# Revit family: Дверь RW 64 двустворчатая. Окрывание наружу
name_source: partatom
category: Окна
revit_build: Autodesk Revit 2016 (Build: 20160314_0715(x64)
units: mm (PartAtom-declared; Revit-internal decimal feet)

## family parameters
Всегда вертикально = Да
Заголовок OmniClass = Windows
Номер OmniClass = 23.30.20.00
Общий = Нет
Основа = Стена
При загрузке вырезать с полостями = Нет
Точка расчета площади = Нет

## types (2) — shared parameters
ADSK_Версия Revit = Revit 2016
ADSK_Единица измерения = шт.
ADSK_Наименование краткое = Дверь RW 64 двустворчатая
Rед = 1.0000 (м²·K)/Вт
Rпрофиля = 1.0000 (м²·K)/Вт
Rстеклопакета = 1.0000 (м²·K)/Вт
URL = http://www.realit.ru
λ краевой зоны стеклопакета = 0.0000 (м²·K)/Вт
Аналитическая конструкция = <Нет>
Высота подоконника по умолчанию = 50 мм
Зазор между створок = 9 мм
Замыкание стены = По основе
Изготовитель = REALIT
Материал-Отлив = REALIT_Отлив_Белый
Материал-Подоконник = REALIT_ПВХ_Белый
Материал-Рама = REALIT_Профиль_RAL 9016
Материал-Стеклопакет = REALIT_Стекло
Монтажный зазор.Боковой = 20 мм
Рама.Высота профиля = 68 мм
Рама.Ширина профиля = 64 мм
Створка.Высота низ.профиля = 142 мм
Створка.Высота профиля = 92 мм
Створка.Ширина профиля = 64 мм
Стеклопакет.Толщина = 48 мм
Толщина стеклопакета = 48
Угол в плане 30° = Нет
Угол в плане 90° = Да
Цвет профиля = RAL 9016
zero-valued in all types: Высота, Примерная высота, Примерная ширина, Ширина

## per-type parameters (varying)
| type | Наименование |
| Дверь RW 64 двустворчатая смещённая. Окрывание наружу. | Дверь RW 64 двустворчатая смещённая. Окрывание: наружу. |
| Дверь RW 64 двустворчатая. Окрывание наружу. | Дверь RW 64 двустворчатая. Окрывание: наружу. |

## geometry (parser evidence)
native form markers: Sweep x1
no freeform markers — native parametric forms only
